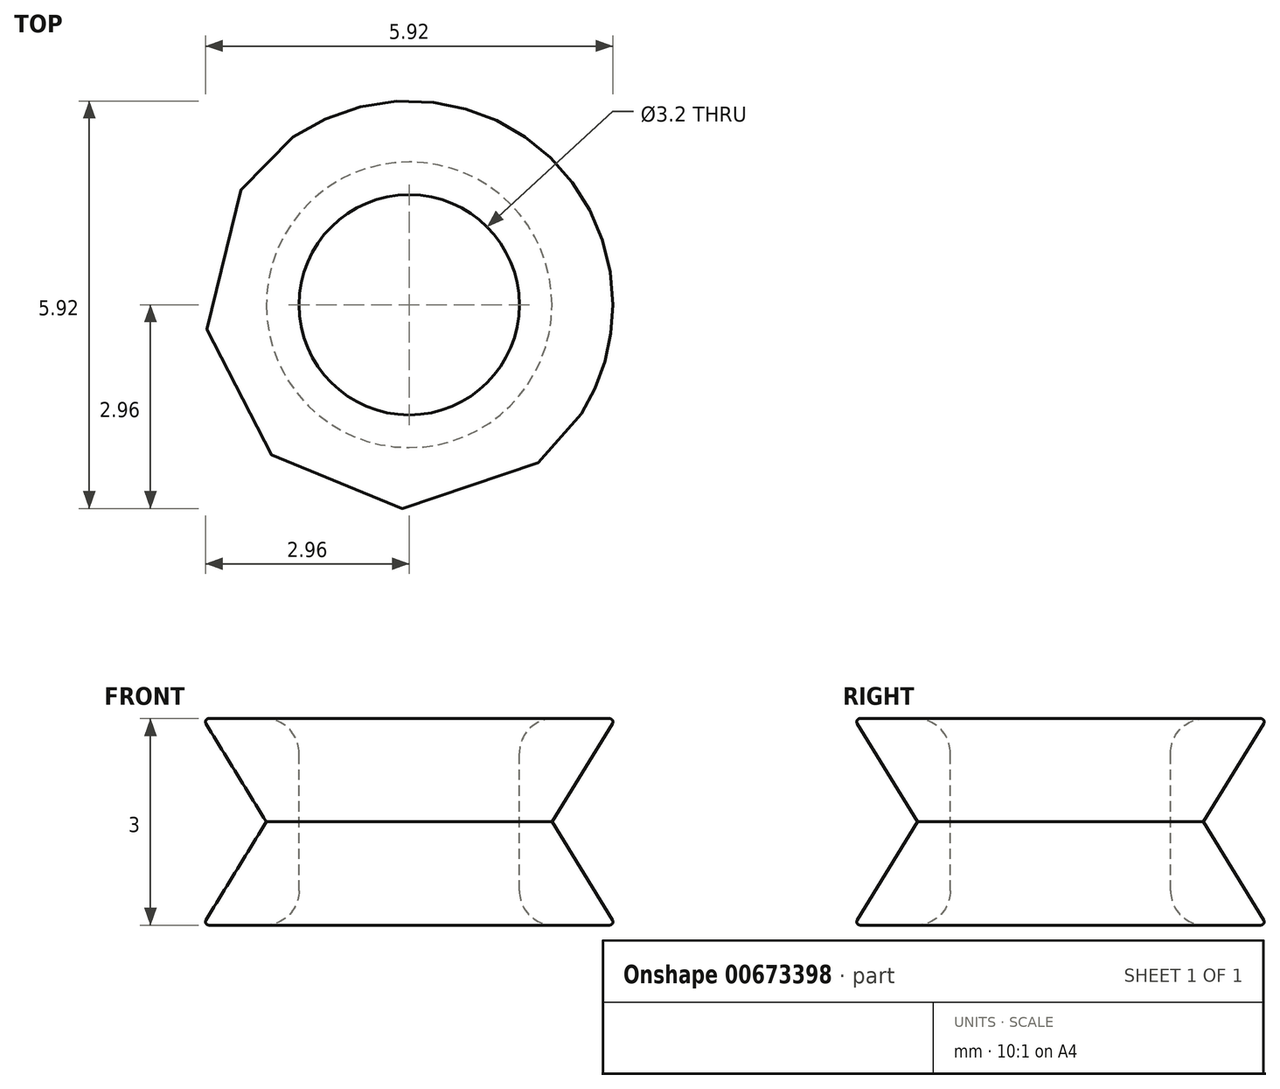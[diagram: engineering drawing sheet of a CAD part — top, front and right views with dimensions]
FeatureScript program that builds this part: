
annotation { "Feature Type Name" : "Feature", "Feature Type Description" : "" }
export const myFeature = defineFeature(function(context is Context, id is Id, definition is map)
    precondition{}
    {
        {
            var Q0;
            Q0=qCreatedBy(makeId("Front.planeOp"),FACE);
            var sketch = newSketch(context, id + "F0", { "sketchPlane" : qUnion([Q0])});
            skLineSegment(sketch, "E0", {"start": v(3, 3) * mm, "end": v(3, -3.08) * mm, "construction": true});
            skLineSegment(sketch, "E1.bottom", {"start": v(1.6, 0) * mm, "end": v(3, 0) * mm});
            skLineSegment(sketch, "E1.top", {"start": v(1.6, 3) * mm, "end": v(3, 3) * mm});
            skLineSegment(sketch, "E2", {"start": v(1.6, 3) * mm, "end": v(1.6, 0) * mm});
            skLineSegment(sketch, "E3", {"start": v(0, 4.53) * mm, "end": v(0, -1.58) * mm, "construction": true});
            skLineSegment(sketch, "E4", {"start": v(3, 3) * mm, "end": v(2.07, 1.5) * mm});
            skPoint(sketch, "E4.endSnap0", {"position": v(1.6, 1.5) * mm});
            skLineSegment(sketch, "E5", {"start": v(2.07, 1.5) * mm, "end": v(3, 0) * mm});
            skSolve(sketch);
        }
        {
            var Q0;
            Q0=makeQuery(id+"F0.imprint","IMPRINT",FACE,{"disambiguationData":[TD([[makeQuery(id+"F0.imprint","IMPRINT",EDGE,{"derivedFrom":sQuery(id+"F0.wireOp",EDGE,"E1.bottom")}),1.0]])]});
            var Q1;
            Q1=sQuery(id+"F0.wireOp",EDGE,"E3");
            revolve(context, id + "F1", {"entities" : qUnion([Q0]), "axis" : qUnion([Q1]), "revolveType" : RevolveType.FULL});
        }
        {
            var Q0;
            Q0=makeQuery(id+"F1.opRevolve","SWEPT_EDGE",EDGE,{"disambiguationData":[OSD([sQuery(id+"F0.wireOp",EDGE,"E1.top"),sQuery(id+"F0.wireOp",EDGE,"E2")])]});
            var Q1;
            Q1=makeQuery(id+"F1.opRevolve","SWEPT_EDGE",EDGE,{"disambiguationData":[OSD([sQuery(id+"F0.wireOp",EDGE,"E1.bottom"),sQuery(id+"F0.wireOp",EDGE,"E2")])]});
            fillet(context, id + "F2", {"entities" : qUnion([Q0, Q1]), "radius" : 0.5 * mm, "tangentPropagation" : true, "allowEdgeOverflow" : false});
        }
        {
            var Q0;
            Q0=makeQuery(id+"F1.opRevolve","SWEPT_EDGE",EDGE,{"disambiguationData":[OSD([sQuery(id+"F0.wireOp",EDGE,"E1.top"),sQuery(id+"F0.wireOp",EDGE,"NEuaabon-mSBI-Ccyf-fmlH-fDRmGJeW8lEB")])]});
            var Q1;
            Q1=makeQuery(id+"F1.opRevolve","SWEPT_EDGE",EDGE,{"disambiguationData":[OSD([sQuery(id+"F0.wireOp",EDGE,"E1.bottom"),sQuery(id+"F0.wireOp",EDGE,"NEuaabon-mSBI-Ccyf-fmlH-fDRmGJeW8lEB")])]});
            fillet(context, id + "F3", {"entities" : qUnion([Q0, Q1]), "radius" : 0.05 * mm, "tangentPropagation" : true, "allowEdgeOverflow" : false});
        }
    });
